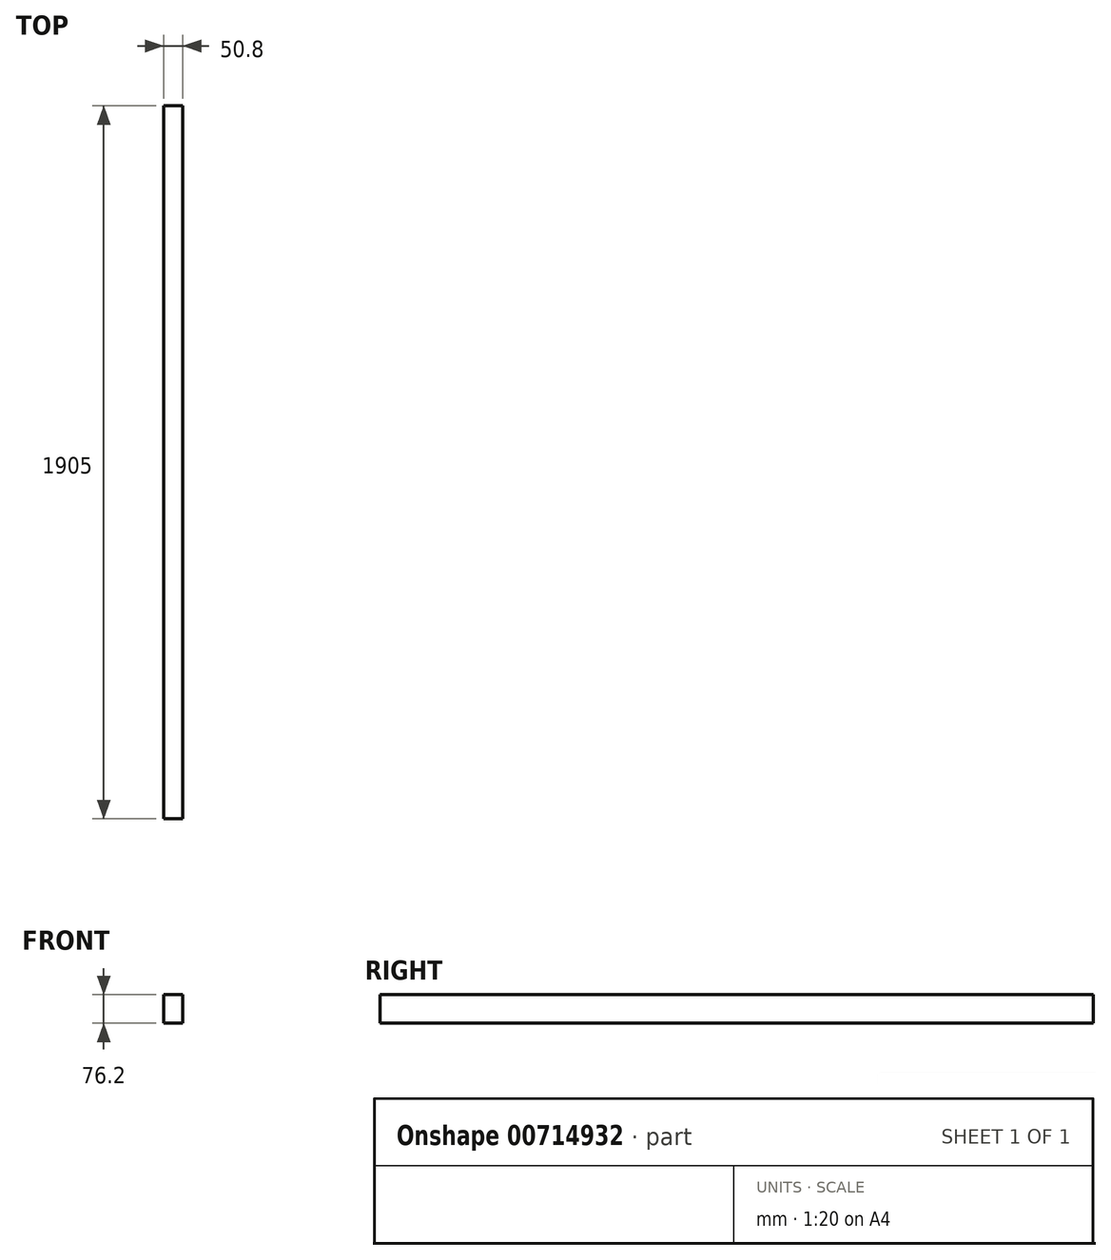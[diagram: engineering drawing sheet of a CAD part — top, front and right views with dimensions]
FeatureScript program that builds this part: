
annotation { "Feature Type Name" : "Feature", "Feature Type Description" : "" }
export const myFeature = defineFeature(function(context is Context, id is Id, definition is map)
    precondition{}
    {
        {
            var Q0;
            Q0=qCreatedBy(makeId("Right.planeOp"),FACE);
            var sketch = newSketch(context, id + "F0", { "sketchPlane" : qUnion([Q0])});
            skLineSegment(sketch, "E0.bottom", {"start": v(1905, 76.2) * mm, "end": v(0, 76.2) * mm});
            skLineSegment(sketch, "E0.top", {"start": v(1905, 0) * mm, "end": v(0, 0) * mm});
            skLineSegment(sketch, "E0.left", {"start": v(1905, 76.2) * mm, "end": v(1905, 0) * mm});
            skLineSegment(sketch, "E0.right", {"start": v(0, 76.2) * mm, "end": v(0, 0) * mm});
            skSolve(sketch);
        }
        {
            var Q0;
            Q0=makeQuery(id+"F0.imprint","IMPRINT",FACE,{"disambiguationData":[TD([[makeQuery(id+"F0.imprint","IMPRINT",EDGE,{"derivedFrom":sQuery(id+"F0.wireOp",EDGE,"E0.bottom")}),1.0]])]});
            extrude(context, id + "F1", {"entities" : qUnion([Q0]), "depth" : 50.8 * mm, "offsetDistance" : 25.4 * mm});
        }
    });
